# Revit family: OLYMP
name_source: partatom
category: Осветительные приборы
revit_build: Autodesk Revit 2016 (Build: 20151007_0715(x64)
units: mm (PartAtom-declared; Revit-internal decimal feet)

## family parameters
Источник света = Да
Общий = Нет
Основа = Грань
При загрузке вырезать с полостями = Да
Размер круглого соединителя = Использовать диаметр
Тип детали = Нормальный
Точка расчета площади = Нет

## types (35) — shared parameters
ADSK_Единица измерения = Шт.
ADSK_Завод-изготовитель = ГК «Вартон»
ADSK_Количество фаз = 1
ADSK_Количество фаз числовое = 1
ADSK_Коэффициент мощности = 0.95
ADSK_Масса = 3.1
ADSK_Напряжение = 220 В
ADSK_Номинальная мощность = 0 кВт
ADSK_Полная мощность = 0 кВ·А
ADSK_Энергоэффективность = 0 лм/Вт
A_tru = 90.00°
IP Class = IP20
URL = http://varton.ru
a = 180.00°
a_dop = 90.00°
sh = 90 мм
Блок аварийного питания = Нет
Видимая форма излучения при визуализации = Нет
Группа модели = Светильники
Изготовитель = ГК «Вартон»
Класс Защиты = I
Класс пожароопасности = нет
Климатическая зона = УХЛ4
Корпус = Корпус белый металл
Область использования = Рекомендован для освещения административных помещений
Плафон = Плафон самосвечение
Полная установленная мощность = 0 кВ·А
Разработчик = ООО ПРОРУБИМ
Разработчик (телефон) = +7 (495) 649-85-43
Разработчик модели (URL) = http://prorubim.com
Светофильтр = 16777215
Смещение цветовой температуры при затухании лампы = <Нет>
Тип ИС = LED
УОИС = УОИС : Светильник светодиодный
Угол наклона = -90.00°
Угол наклона светильника = 90.00°
zero-valued in all types: sm1, sm2, Отметка по умолчанию

## per-type parameters (varying)
| type | ADSK_Наименование | ADSK_Размер_Высота | ADSK_Размер_Длина | ADSK_Размер_Ширина | ADSK_Ток | h | Излучение по длине прямоугольника | Излучение по ширине прямоугольника | Описание | Тип продукции | Файл фотометрической сетки |
| V1-I0-70076-04L10-6506050 | Светодиодный светильник ВАРТОН промышленный Olymp 12° 55 Вт 5000 К | 262 мм | 320 мм | 211 мм | 0 А | 172 мм | 211 мм | 320 мм | Светодиодный светильник ВАРТОН промышленный Olymp 12° 55 Вт 5000 К | Светодиодный светильник ВАРТОН промышленный Olymp 12° 55 Вт 5000 К | V1-I0-70076-04L10-650605012deg.ies |
| V1-I0-70077-04L10-6509050 | Светодиодный светильник ВАРТОН промышленный Olymp 12° 80 Вт 5000 К | 262 мм | 426 мм | 211 мм | 0 А | 172 мм | 211 мм | 426 мм | Светодиодный светильник ВАРТОН промышленный Olymp 12° 80 Вт 5000 К | Светодиодный светильник ВАРТОН промышленный Olymp 12° 80 Вт 5000 К | V1-I0-70076-04L10-650605012deg.ies |
| V1-I0-70077-04L10-6512050 | Светодиодный светильник ВАРТОН промышленный Olymp 12° 110 Вт 5000 К | 262 мм | 426 мм | 211 мм | 1 А | 172 мм | 211 мм | 426 мм | Светодиодный светильник ВАРТОН промышленный Olymp 12° 110 Вт 5000 К | Светодиодный светильник ВАРТОН промышленный Olymp 12° 110 Вт 5000 К | V1-I0-70076-04L10-650605012deg.ies |
| V1-I0-70078-04L10-6515050 | Светодиодный светильник ВАРТОН промышленный Olymp 12° 135 Вт 5000 К | 262 мм | 546 мм | 211 мм | 1 А | 172 мм | 211 мм | 546 мм | Светодиодный светильник ВАРТОН промышленный Olymp 12° 135 Вт 5000 К | Светодиодный светильник ВАРТОН промышленный Olymp 12° 135 Вт 5000 К | V1-I0-70076-04L10-650605012deg.ies |
| V1-I0-70096-04L10-6518050 | Светодиодный светильник ВАРТОН промышленный Olymp 12° 160 Вт 5000 К | 347 мм | 426 мм | 431 мм | 1 А | 257 мм | 431 мм | 426 мм | Светодиодный светильник ВАРТОН промышленный Olymp 12° 160 Вт 5000 К | Светодиодный светильник ВАРТОН промышленный Olymp 12° 160 Вт 5000 К | V1-I0-70076-04L10-650605012deg.ies |
| V1-I0-70096-04L10-6524050 | Светодиодный светильник ВАРТОН промышленный Olymp 12° 215 Вт 5000 К | 347 мм | 426 мм | 431 мм | 1 А | 257 мм | 431 мм | 426 мм | Светодиодный светильник ВАРТОН промышленный Olymp 12° 215 Вт 5000 К | Светодиодный светильник ВАРТОН промышленный Olymp 12° 215 Вт 5000 К | V1-I0-70076-04L10-650605012deg.ies |
| V1-I0-70097-04L10-6530050 | Светодиодный светильник ВАРТОН промышленный Olymp 12° 275 Вт 5000 К | 347 мм | 546 мм | 431 мм | 1 А | 257 мм | 431 мм | 546 мм | Светодиодный светильник ВАРТОН промышленный Olymp 12° 275 Вт 5000 К | Светодиодный светильник ВАРТОН промышленный Olymp 12° 275 Вт 5000 К | V1-I0-70076-04L10-650605012deg.ies |
| V1-I0-70076-04L09-6506050 | Светодиодный светильник ВАРТОН промышленный Olymp 19° 55 Вт 5000 К | 262 мм | 320 мм | 211 мм | 0 А | 172 мм | 211 мм | 320 мм | Светодиодный светильник ВАРТОН промышленный Olymp 19° 55 Вт 5000 К | Светодиодный светильник ВАРТОН промышленный Olymp 19° 55 Вт 5000 К | V1-I0-70076-04L09-650605019deg.ies |
| V1-I0-70077-04L09-6509050 | Светодиодный светильник ВАРТОН промышленный Olymp 19° 80 Вт 5000 К | 262 мм | 426 мм | 211 мм | 0 А | 172 мм | 211 мм | 426 мм | Светодиодный светильник ВАРТОН промышленный Olymp 19° 80 Вт 5000 К | Светодиодный светильник ВАРТОН промышленный Olymp 19° 80 Вт 5000 К | V1-I0-70076-04L09-650605019deg.ies |
| V1-I0-70077-04L09-6512050 | Светодиодный светильник ВАРТОН промышленный Olymp 19° 110 Вт 5000 К | 262 мм | 426 мм | 211 мм | 1 А | 172 мм | 211 мм | 426 мм | Светодиодный светильник ВАРТОН промышленный Olymp 19° 110 Вт 5000 К | Светодиодный светильник ВАРТОН промышленный Olymp 19° 110 Вт 5000 К | V1-I0-70076-04L09-650605019deg.ies |
| V1-I0-70078-04L09-6515050 | Светодиодный светильник ВАРТОН промышленный Olymp 19° 135 Вт 5000 К | 262 мм | 546 мм | 211 мм | 1 А | 172 мм | 211 мм | 546 мм | Светодиодный светильник ВАРТОН промышленный Olymp 19° 135 Вт 5000 К | Светодиодный светильник ВАРТОН промышленный Olymp 19° 135 Вт 5000 К | V1-I0-70076-04L09-650605019deg.ies |
| V1-I0-70096-04L09-6518050 | Светодиодный светильник ВАРТОН промышленный Olymp 19° 160 Вт 5000 К | 347 мм | 426 мм | 431 мм | 1 А | 257 мм | 431 мм | 426 мм | Светодиодный светильник ВАРТОН промышленный Olymp 19° 160 Вт 5000 К | Светодиодный светильник ВАРТОН промышленный Olymp 19° 160 Вт 5000 К | V1-I0-70076-04L09-650605019deg.ies |
| V1-I0-70096-04L09-6524050 | Светодиодный светильник ВАРТОН промышленный Olymp 19° 215 Вт 5000 К | 347 мм | 426 мм | 431 мм | 1 А | 257 мм | 431 мм | 426 мм | Светодиодный светильник ВАРТОН промышленный Olymp 19° 215 Вт 5000 К | Светодиодный светильник ВАРТОН промышленный Olymp 19° 215 Вт 5000 К | V1-I0-70076-04L09-650605019deg.ies |
| V1-I0-70097-04L09-6530050 | Светодиодный светильник ВАРТОН промышленный Olymp 19° 275 Вт 5000 К | 347 мм | 546 мм | 431 мм | 1 А | 257 мм | 431 мм | 546 мм | Светодиодный светильник ВАРТОН промышленный Olymp 19° 275 Вт 5000 К | Светодиодный светильник ВАРТОН промышленный Olymp 19° 275 Вт 5000 К | V1-I0-70076-04L09-650605019deg.ies |
| V1-I0-70076-04L07-6506050 | Светодиодный светильник ВАРТОН промышленный Olymp 60° 55 Вт 5000 К | 262 мм | 320 мм | 211 мм | 0 А | 172 мм | 211 мм | 320 мм | Светодиодный светильник ВАРТОН промышленный Olymp 60° 55 Вт 5000 К | Светодиодный светильник ВАРТОН промышленный Olymp 60° 55 Вт 5000 К | V1-I0-70076-04L07-650605060deg.ies |
| V1-I0-70077-04L07-6509050 | Светодиодный светильник ВАРТОН промышленный Olymp 60° 80 Вт 5000 К | 262 мм | 426 мм | 211 мм | 0 А | 172 мм | 211 мм | 426 мм | Светодиодный светильник ВАРТОН промышленный Olymp 60° 80 Вт 5000 К | Светодиодный светильник ВАРТОН промышленный Olymp 60° 80 Вт 5000 К | V1-I0-70076-04L07-650605060deg.ies |
| V1-I0-70077-04L07-6512050 | Светодиодный светильник ВАРТОН промышленный Olymp 60° 110 Вт 5000 К | 262 мм | 426 мм | 211 мм | 1 А | 172 мм | 211 мм | 426 мм | Светодиодный светильник ВАРТОН промышленный Olymp 60° 110 Вт 5000 К | Светодиодный светильник ВАРТОН промышленный Olymp 60° 110 Вт 5000 К | V1-I0-70076-04L07-650605060deg.ies |
| V1-I0-70078-04L07-6515050 | Светодиодный светильник ВАРТОН промышленный Olymp 60° 135 Вт 5000 К | 262 мм | 546 мм | 211 мм | 1 А | 172 мм | 211 мм | 546 мм | Светодиодный светильник ВАРТОН промышленный Olymp 60° 135 Вт 5000 К | Светодиодный светильник ВАРТОН промышленный Olymp 60° 135 Вт 5000 К | V1-I0-70076-04L07-650605060deg.ies |
| V1-I0-70096-04L07-6518050 | Светодиодный светильник ВАРТОН промышленный Olymp 60° 160 Вт 5000 К | 347 мм | 426 мм | 431 мм | 1 А | 257 мм | 431 мм | 426 мм | Светодиодный светильник ВАРТОН промышленный Olymp 60° 160 Вт 5000 К | Светодиодный светильник ВАРТОН промышленный Olymp 60° 160 Вт 5000 К | V1-I0-70076-04L07-650605060deg.ies |
| V1-I0-70096-04L07-6524050 | Светодиодный светильник ВАРТОН промышленный Olymp 60° 215 Вт 5000 К | 347 мм | 426 мм | 431 мм | 1 А | 257 мм | 431 мм | 426 мм | Светодиодный светильник ВАРТОН промышленный Olymp 60° 215 Вт 5000 К | Светодиодный светильник ВАРТОН промышленный Olymp 60° 215 Вт 5000 К | V1-I0-70076-04L07-650605060deg.ies |
| V1-I0-70097-04L07-6530050 | Светодиодный светильник ВАРТОН промышленный Olymp 60° 275 Вт 5000 К | 347 мм | 546 мм | 431 мм | 1 А | 257 мм | 431 мм | 546 мм | Светодиодный светильник ВАРТОН промышленный Olymp 60° 275 Вт 5000 К | Светодиодный светильник ВАРТОН промышленный Olymp 60° 275 Вт 5000 К | V1-I0-70076-04L07-650605060deg.ies |
| V1-I0-70076-04L06-6506050 | Светодиодный светильник ВАРТОН промышленный Olymp 90° 55 Вт 5000 К | 262 мм | 320 мм | 211 мм | 0 А | 172 мм | 211 мм | 320 мм | Светодиодный светильник ВАРТОН промышленный Olymp 90° 55 Вт 5000 К | Светодиодный светильник ВАРТОН промышленный Olymp 90° 55 Вт 5000 К | V1-I0-70076-04L06-650605090deg.ies |
| V1-I0-70077-04L06-6509050 | Светодиодный светильник ВАРТОН промышленный Olymp 90° 80 Вт 5000 К | 262 мм | 426 мм | 211 мм | 0 А | 172 мм | 211 мм | 426 мм | Светодиодный светильник ВАРТОН промышленный Olymp 90° 80 Вт 5000 К | Светодиодный светильник ВАРТОН промышленный Olymp 90° 80 Вт 5000 К | V1-I0-70076-04L06-650605090deg.ies |
| V1-I0-70077-04L06-6512050 | Светодиодный светильник ВАРТОН промышленный Olymp 90° 110 Вт 5000 К | 262 мм | 426 мм | 211 мм | 1 А | 172 мм | 211 мм | 426 мм | Светодиодный светильник ВАРТОН промышленный Olymp 90° 110 Вт 5000 К | Светодиодный светильник ВАРТОН промышленный Olymp 90° 110 Вт 5000 К | V1-I0-70076-04L06-650605090deg.ies |
| V1-I0-70078-04L06-6515050 | Светодиодный светильник ВАРТОН промышленный Olymp 90° 135 Вт 5000 К | 262 мм | 546 мм | 211 мм | 1 А | 172 мм | 211 мм | 546 мм | Светодиодный светильник ВАРТОН промышленный Olymp 90° 135 Вт 5000 К | Светодиодный светильник ВАРТОН промышленный Olymp 90° 135 Вт 5000 К | V1-I0-70076-04L06-650605090deg.ies |
| V1-I0-70096-04L06-6518050 | Светодиодный светильник ВАРТОН промышленный Olymp 90° 160 Вт 5000 К | 347 мм | 426 мм | 431 мм | 1 А | 257 мм | 431 мм | 426 мм | Светодиодный светильник ВАРТОН промышленный Olymp 90° 160 Вт 5000 К | Светодиодный светильник ВАРТОН промышленный Olymp 90° 160 Вт 5000 К | V1-I0-70076-04L06-650605090deg.ies |
| V1-I0-70096-04L06-6524050 | Светодиодный светильник ВАРТОН промышленный Olymp 90° 215 Вт 5000 К | 347 мм | 426 мм | 431 мм | 1 А | 257 мм | 431 мм | 426 мм | Светодиодный светильник ВАРТОН промышленный Olymp 90° 215 Вт 5000 К | Светодиодный светильник ВАРТОН промышленный Olymp 90° 215 Вт 5000 К | V1-I0-70076-04L06-650605090deg.ies |
| V1-I0-70097-04L06-6530050 | Светодиодный светильник ВАРТОН промышленный Olymp 90° 275 Вт 5000 К | 347 мм | 546 мм | 431 мм | 1 А | 257 мм | 431 мм | 546 мм | Светодиодный светильник ВАРТОН промышленный Olymp 90° 275 Вт 5000 К | Светодиодный светильник ВАРТОН промышленный Olymp 90° 275 Вт 5000 К | V1-I0-70076-04L06-650605090deg.ies |
| V1-I0-70076-04L08-6506050 | Светодиодный светильник ВАРТОН промышленный Olymp 30°х110° 55 Вт 5000 К | 262 мм | 320 мм | 211 мм | 0 А | 172 мм | 211 мм | 320 мм | Светодиодный светильник ВАРТОН промышленный Olymp 30°х110° 55 Вт 5000 К | Светодиодный светильник ВАРТОН промышленный Olymp 30°х110° 55 Вт 5000 К | V1-I0-70076-04L08-650605030deg110deg.ies |
| V1-I0-70077-04L08-6509050 | Светодиодный светильник ВАРТОН промышленный Olymp 30°х110° 80 Вт 5000 К | 262 мм | 426 мм | 211 мм | 0 А | 172 мм | 211 мм | 426 мм | Светодиодный светильник ВАРТОН промышленный Olymp 30°х110° 80 Вт 5000 К | Светодиодный светильник ВАРТОН промышленный Olymp 30°х110° 80 Вт 5000 К | V1-I0-70076-04L08-650605030deg110deg.ies |
| V1-I0-70077-04L08-6512050 | Светодиодный светильник ВАРТОН промышленный Olymp 30°х110° 110 Вт 5000 К | 262 мм | 426 мм | 211 мм | 1 А | 172 мм | 211 мм | 426 мм | Светодиодный светильник ВАРТОН промышленный Olymp 30°х110° 110 Вт 5000 К | Светодиодный светильник ВАРТОН промышленный Olymp 30°х110° 110 Вт 5000 К | V1-I0-70076-04L08-650605030deg110deg.ies |
| V1-I0-70078-04L08-6515050 | Светодиодный светильник ВАРТОН промышленный Olymp 30°х110° 135 Вт 5000 К | 262 мм | 546 мм | 211 мм | 1 А | 172 мм | 211 мм | 546 мм | Светодиодный светильник ВАРТОН промышленный Olymp 30°х110° 135 Вт 5000 К | Светодиодный светильник ВАРТОН промышленный Olymp 30°х110° 135 Вт 5000 К | V1-I0-70076-04L08-650605030deg110deg.ies |
| V1-I0-70096-04L08-6518050 | Светодиодный светильник ВАРТОН промышленный Olymp 30°х110° 160 Вт 5000 К | 347 мм | 426 мм | 431 мм | 1 А | 257 мм | 431 мм | 426 мм | Светодиодный светильник ВАРТОН промышленный Olymp 30°х110° 160 Вт 5000 К | Светодиодный светильник ВАРТОН промышленный Olymp 30°х110° 160 Вт 5000 К | V1-I0-70076-04L08-650605030deg110deg.ies |
| V1-I0-70096-04L08-6524050 | Светодиодный светильник ВАРТОН промышленный Olymp 30°х110° 215 Вт 5000 К | 347 мм | 426 мм | 431 мм | 1 А | 257 мм | 431 мм | 426 мм | Светодиодный светильник ВАРТОН промышленный Olymp 30°х110° 215 Вт 5000 К | Светодиодный светильник ВАРТОН промышленный Olymp 30°х110° 215 Вт 5000 К | V1-I0-70076-04L08-650605030deg110deg.ies |
| V1-I0-70097-04L08-6530050 | Светодиодный светильник ВАРТОН промышленный Olymp 30°х110° 275 Вт 5000 К | 347 мм | 546 мм | 431 мм | 1 А | 257 мм | 431 мм | 546 мм | Светодиодный светильник ВАРТОН промышленный Olymp 30°х110° 275 Вт 5000 К | Светодиодный светильник ВАРТОН промышленный Olymp 30°х110° 275 Вт 5000 К | V1-I0-70076-04L08-650605030deg110deg.ies |

note: column(s) folded — value = type name in every type: ADSK_Код изделия

## geometry (parser evidence)
native form markers: Blend x2
no freeform markers — native parametric forms only
